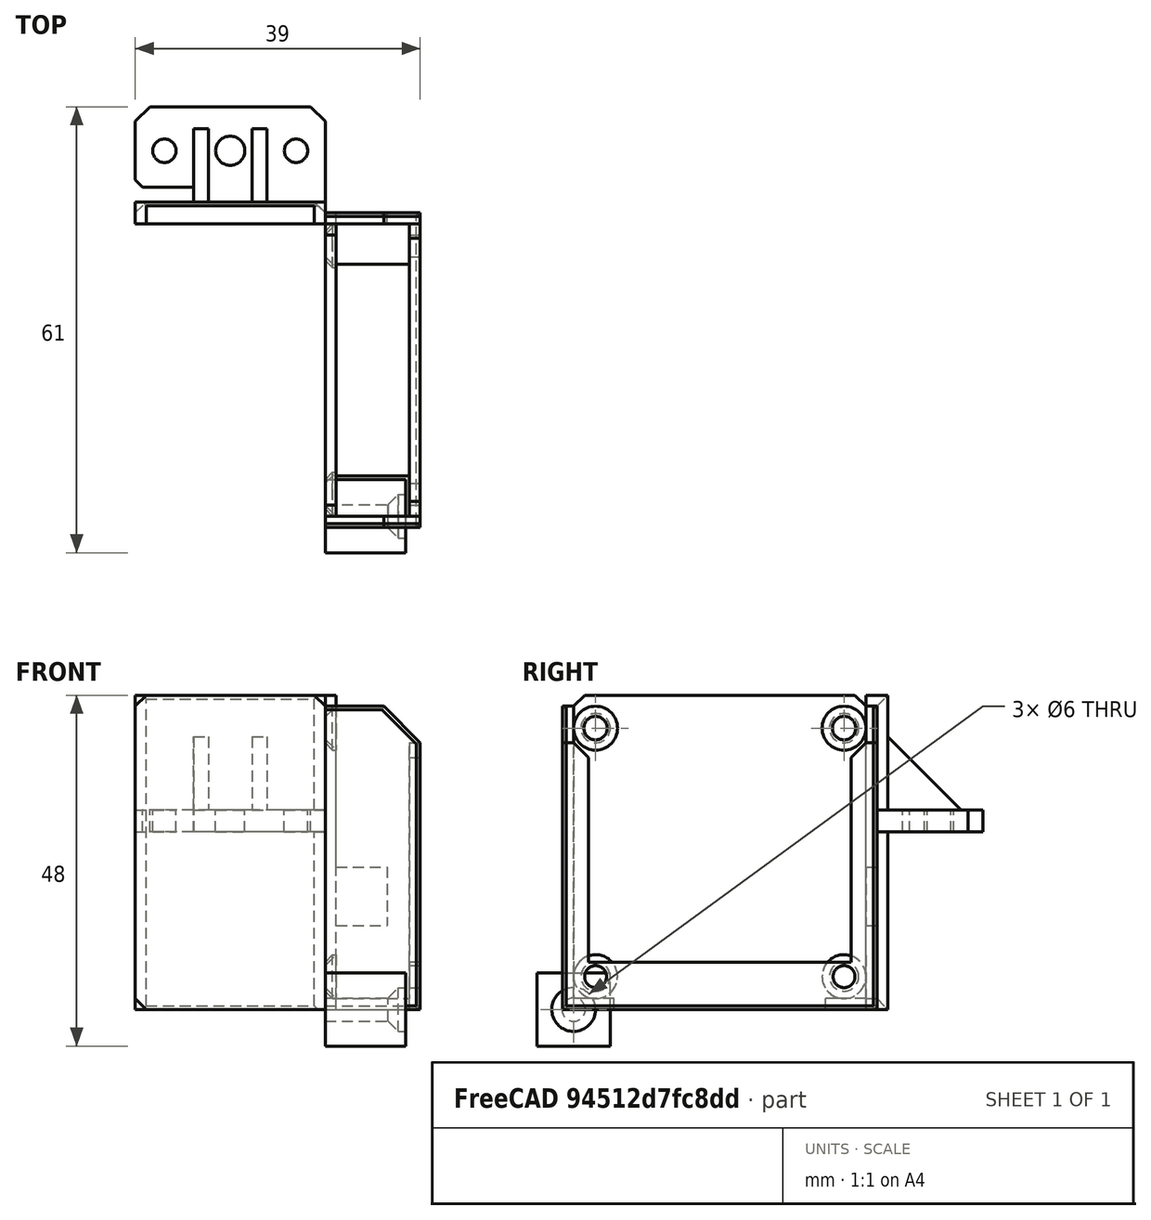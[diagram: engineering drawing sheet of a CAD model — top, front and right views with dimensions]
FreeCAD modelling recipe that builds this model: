
FCSTD DOCUMENT  (FreeCAD 0.18R14555 (Git shallow))
Label: hemera-duct
License: All rights reserved
LicenseURL: http://en.wikipedia.org/wiki/All_rights_reserved
objects: Part::Box×16, Part::Chamfer×11, Part::Feature×9, Part::Cut×9, Part::Cylinder×8, Part::MultiFuse×6, Part::MultiCommon×1
note: 60 computed .brp shape members not serialized (recipe doc carries the construction recipe); baked Part::Feature solids carry a one-line shape summary decoded from their .brp

FEATURE [Part::Feature] Hemera_Ender_3_Part_Cooling001
  Placement = pos=(2.11,-0.04,0.21) rot=(0,0,1;0rad)
  shape: bbox 45.78 x 43.07 x 60.57 mm, 15650 faces, 0 solids (baked)
FEATURE [Part::Box] Box001  label="40-base001"
  AttacherType = Attacher::AttachEngine3D
  Height = 42
  Length = 3.5
  Placement = pos=(-1,-1,0) rot=(0,0,1;0rad)
  Width = 42
FEATURE [Part::Cut] Cut  label="nozzle"
  Base = -> Hemera_Ender_3_Part_Cooling001
  Placement = pos=(0,0,1.5) rot=(0,0,1;0rad)
  Tool = -> Box001
FEATURE [Part::Box] Box  label="43-base"
  AttacherType = Attacher::AttachEngine3D
  Height = 43
  Length = 1.5
  Width = 40
FEATURE [Part::Cylinder] Cylinder
  Angle = 360
  AttacherType = Attacher::AttachEngine3D
  Height = 10
  Placement = pos=(-1e-15,3,4.5) rot=(0,1,0;1.5708rad)
  Radius = 1.6
FEATURE [Part::Cylinder] Cylinder001
  Angle = 360
  AttacherType = Attacher::AttachEngine3D
  Height = 10
  Placement = pos=(-1e-15,37,4.5) rot=(0,1,0;1.5708rad)
  Radius = 1.6
FEATURE [Part::Cylinder] Cylinder002
  Angle = 360
  AttacherType = Attacher::AttachEngine3D
  Height = 10
  Placement = pos=(-9e-15,3,38.5) rot=(0,1,0;1.5708rad)
  Radius = 1.6
FEATURE [Part::Cylinder] Cylinder003
  Angle = 360
  AttacherType = Attacher::AttachEngine3D
  Height = 10
  Placement = pos=(-9e-15,37,38.5) rot=(0,1,0;1.5708rad)
  Radius = 1.6
FEATURE [Part::Box] Box002  label="43-base001"
  AttacherType = Attacher::AttachEngine3D
  Height = 43
  Length = 7.5
  Placement = pos=(0,-1,0) rot=(0,0,1;0rad)
  Width = 42
FEATURE [Part::MultiFuse] Fusion
  Shapes = -> [Cylinder003,Cylinder001,Cylinder002,Cylinder]
FEATURE [Part::Cut] Cut001
  Base = -> Box002
  Tool = -> Fusion
FEATURE [Part::Chamfer] Chamfer
  Base = -> Cut001
  Edges = 4 edges r=1.4: [Edge17,Edge19,Edge21,Edge23]
  Placement = pos=(-6,0,0) rot=(0,0,1;0rad)
FEATURE [Part::MultiCommon] Common
  Shapes = -> [Box,Chamfer]
FEATURE [Part::Box] Box003  label="Cube"
  AttacherType = Attacher::AttachEngine3D
  Height = 1.5
  Length = 13
  Placement = pos=(0,-1.5,0) rot=(0,0,1;0rad)
  Width = 7
FEATURE [Part::Box] Box004  label="Cube001"
  AttacherType = Attacher::AttachEngine3D
  Height = 1.5
  Length = 13
  Placement = pos=(0,34.5,0) rot=(0,0,1;0rad)
  Width = 7
FEATURE [Part::Box] Box005  label="Cube002"
  AttacherType = Attacher::AttachEngine3D
  Height = 6.5
  Length = 1.5
  Placement = pos=(11.5,-1.5,0) rot=(0,0,1;0rad)
  Width = 43
FEATURE [Part::Box] Box006  label="Cube003"
  AttacherType = Attacher::AttachEngine3D
  Height = 41.5
  Length = 13
  Placement = pos=(0,-1.5,0) rot=(0,0,1;0rad)
  Width = 1.5
FEATURE [Part::Box] Box007  label="Cube004"
  AttacherType = Attacher::AttachEngine3D
  Height = 41.5
  Length = 13
  Placement = pos=(0,40,0) rot=(0,0,1;0rad)
  Width = 1.5
FEATURE [Part::Box] Box008  label="Cube005"
  AttacherType = Attacher::AttachEngine3D
  Height = 36.5
  Length = 1.5
  Placement = pos=(11.5,-1.5,0) rot=(0,0,1;0rad)
  Width = 3.5
FEATURE [Part::Box] Box009  label="Cube006"
  AttacherType = Attacher::AttachEngine3D
  Height = 36.5
  Length = 1.5
  Placement = pos=(11.5,38,0) rot=(0,0,1;0rad)
  Width = 3.5
FEATURE [Part::Chamfer] Chamfer001
  Base = -> Common
  Edges = 2 edges r=1.5: [Edge13,Edge14]
FEATURE [Part::Chamfer] Chamfer002
  Base = -> Box006
  Edges = 1 edges r=5: [Edge6]
FEATURE [Part::Chamfer] Chamfer003
  Base = -> Box007
  Edges = 1 edges r=5: [Edge6]
FEATURE [Part::Chamfer] Chamfer004
  Base = -> Box008
  Edges = 1 edges r=2: [Edge12]
FEATURE [Part::Chamfer] Chamfer005
  Base = -> Box009
  Edges = 1 edges r=2: [Edge10]
FEATURE [Part::MultiFuse] Fusion001
  Shapes = -> [Chamfer005,Chamfer002,Chamfer003,Chamfer001,Box005,Chamfer004,Box004,Box003]
FEATURE [Part::Cylinder] Cylinder004
  Angle = 360
  AttacherType = Attacher::AttachEngine3D
  Height = 5
  Placement = pos=(9.5,3,4.5) rot=(0,1,0;1.5708rad)
  Radius = 1.5
FEATURE [Part::Cylinder] Cylinder005
  Angle = 360
  AttacherType = Attacher::AttachEngine3D
  Height = 5
  Placement = pos=(9.5,37,4.5) rot=(0,1,0;1.5708rad)
  Radius = 1.5
FEATURE [Part::MultiFuse] Fusion002
  Shapes = -> [Cylinder005,Cylinder004]
FEATURE [Part::Cut] Cut002
  Base = -> Fusion001
  Tool = -> Fusion002
FEATURE [Part::Feature] Cut002001  label="Cut003"
  shape: bbox 13 x 43 x 43 mm, 37 faces (baked)
FEATURE [Part::Chamfer] Chamfer006
  Base = -> Cut002001
  Edges = 5 edges r=0.5: [Edge90,Edge91,Edge92,Edge108,Edge110]
FEATURE [Part::Chamfer] Chamfer007
  Base = -> Chamfer006
  Edges = 4 edges r=0.5: [Edge1,Edge7,Edge54,Edge108]
FEATURE [Part::Box] Box010  label="Cube007"
  AttacherType = Attacher::AttachEngine3D
  Height = 8
  Length = 7
  Placement = pos=(1.5,32.5,11.5) rot=(0,0,1;0rad)
  Width = 10
FEATURE [Part::Cut] Cut002002  label="pt-2"
  Base = -> Chamfer007
  Tool = -> Box010
FEATURE [Part::Feature] Chamfer001004001001  label="Chamfer001006"
  Placement = pos=(8.9e-15,40,0) rot=(0,0,1;1.5708rad)
  shape: bbox 26 x 21.9 x 43 mm, 43 faces (baked)
FEATURE [Part::Box] Box011  label="Cube008"
  AttacherType = Attacher::AttachEngine3D
  Height = 43
  Length = 26
  Placement = pos=(-26,40,0) rot=(0,0,1;0rad)
  Width = 3
FEATURE [Part::Box] Box012  label="Cube009"
  AttacherType = Attacher::AttachEngine3D
  Height = 43
  Length = 26
  Placement = pos=(-26,33,0) rot=(0,0,1;0rad)
  Width = 7
FEATURE [Part::MultiFuse] Fusion003
  Shapes = -> [Box011,Chamfer001004001001]
FEATURE [Part::Cut] Cut002003
  Base = -> Fusion003
  Tool = -> Box012
FEATURE [Part::Feature] Cut002003001  label="Cut002004"
  shape: bbox 26 x 16 x 43 mm, 23 faces (baked)
FEATURE [Part::Chamfer] Chamfer001004001002
  Base = -> Cut002003001
  Edges = 6 edges r=1.5: [Edge2,Edge3,Edge4,Edge10,Edge20,Edge63]
FEATURE [Part::Chamfer] Chamfer001004001003  label="pt-1"
  Base = -> Chamfer001004001002
  Edges = 2 edges r=0.5: [Edge16,Edge29]
FEATURE [Part::Cylinder] Cylinder006
  Angle = 360
  AttacherType = Attacher::AttachEngine3D
  Height = 10
  Placement = pos=(0,0,0) rot=(0,1,0;1.5708rad)
  Radius = 1.6
FEATURE [Part::Box] Box013  label="Cube010"
  AttacherType = Attacher::AttachEngine3D
  Height = 10
  Length = 10
  Placement = pos=(0,-5,-5) rot=(0,0,1;0rad)
  Width = 10
FEATURE [Part::Cylinder] Cylinder007
  Angle = 360
  AttacherType = Attacher::AttachEngine3D
  Height = 10
  Placement = pos=(5,0,1.1e-15) rot=(0,1,0;1.5708rad)
  Radius = 3
FEATURE [Part::Cut] Cut002003002
  Base = -> Box013
  Tool = -> Cylinder006
FEATURE [Part::Chamfer] Chamfer001004001004
  Base = -> Cut002003002
  Edges = 1 edges r=1.4: [Edge14]
FEATURE [Part::Box] Box014  label="Cube011"
  AttacherType = Attacher::AttachEngine3D
  Height = 10
  Length = 1
  Placement = pos=(10,-5,-5) rot=(0,0,1;0rad)
  Width = 10
FEATURE [Part::Cut] Cut002003003
  Base = -> Box014
  Tool = -> Cylinder007
FEATURE [Part::MultiFuse] Fusion004
  Shapes = -> [Cut002003003,Chamfer001004001004]
FEATURE [Part::Feature] Fusion004001  label="Fusion005"
  shape: bbox 11 x 10 x 10 mm, 9 faces (baked)
FEATURE [Part::Box] Box015  label="Cube012"
  AttacherType = Attacher::AttachEngine3D
  Height = 10
  Length = 11
  Placement = pos=(0,-5,-5) rot=(0,0,1;0rad)
  Width = 10
FEATURE [Part::Cut] Cut002003004  label="screw"
  Base = -> Box015
  Tool = -> Fusion004001
FEATURE [Part::Feature] Cut002003004001  label="screw001"
  Placement = pos=(-9,3,4.5) rot=(0,0,1;0rad)
  shape: bbox 11 x 6 x 6 mm, 5 faces (baked)
FEATURE [Part::Feature] Cut002003004002  label="screw002"
  Placement = pos=(-9,37,4.5) rot=(0,0,1;0rad)
  shape: bbox 11 x 6 x 6 mm, 5 faces (baked)
FEATURE [Part::Feature] Cut002003004003  label="screw003"
  Placement = pos=(-9,37,38.5) rot=(0,0,1;0rad)
  shape: bbox 11 x 6 x 6 mm, 5 faces (baked)
FEATURE [Part::Feature] Cut002003004004  label="screw004"
  Placement = pos=(-9,3,38.5) rot=(0,0,1;0rad)
  shape: bbox 11 x 6 x 6 mm, 5 faces (baked)
FEATURE [Part::MultiFuse] Fusion004002
  Shapes = -> [Cut002003004001,Cut002003004004,Cut002003004003,Cut002003004002]
FEATURE [Part::Cut] Cut002003004005
  Base = -> Cut002002
  Tool = -> Fusion004002
